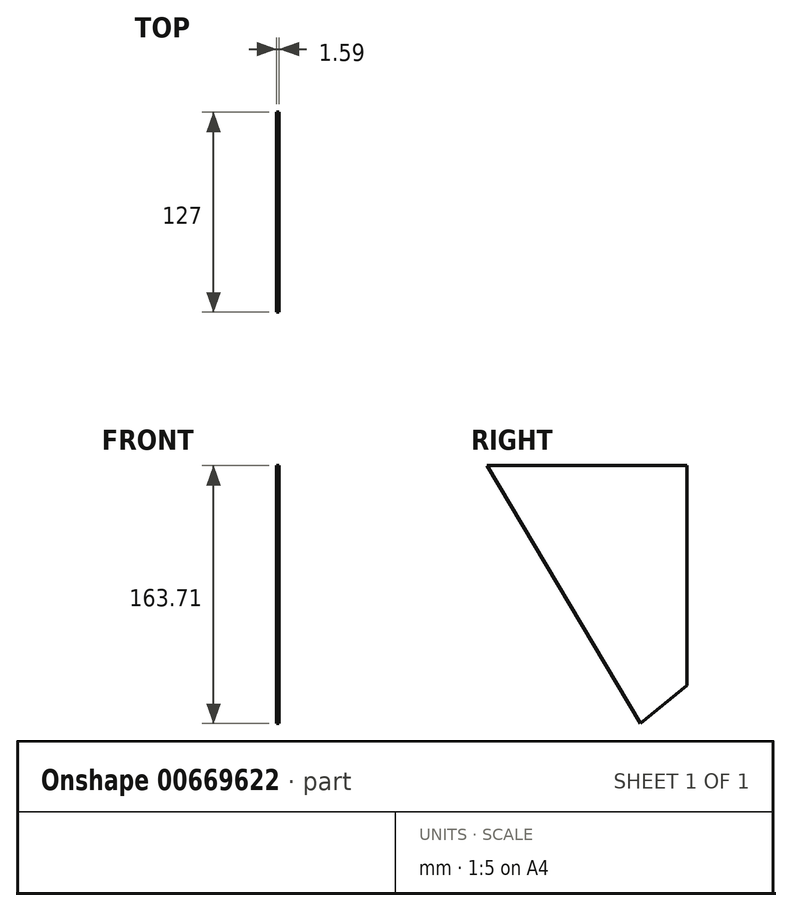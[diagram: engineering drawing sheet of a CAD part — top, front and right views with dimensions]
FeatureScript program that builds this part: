
annotation { "Feature Type Name" : "Feature", "Feature Type Description" : "" }
export const myFeature = defineFeature(function(context is Context, id is Id, definition is map)
    precondition{}
    {
        {
            var Q0;
            Q0=qCreatedBy(makeId("Right.planeOp"),FACE);
            var sketch = newSketch(context, id + "F0", { "sketchPlane" : qUnion([Q0])});
            skLineSegment(sketch, "E0", {"start": v(-52.77, 69.54) * mm, "end": v(74.23, 69.54) * mm});
            skLineSegment(sketch, "E1", {"start": v(74.23, 69.54) * mm, "end": v(74.23, -70.16) * mm});
            skLineSegment(sketch, "E2", {"start": v(74.23, -70.16) * mm, "end": v(44.64, -94.17) * mm});
            skLineSegment(sketch, "E3", {"start": v(44.64, -94.17) * mm, "end": v(-52.77, 69.54) * mm});
            skSolve(sketch);
        }
        {
            var Q0;
            Q0 = qSketchRegion(id + "F0", true);
            extrude(context, id + "F1", {"entities" : qUnion([Q0]), "depth" : 1.59 * mm, "offsetDistance" : 25.4 * mm});
        }
    });
